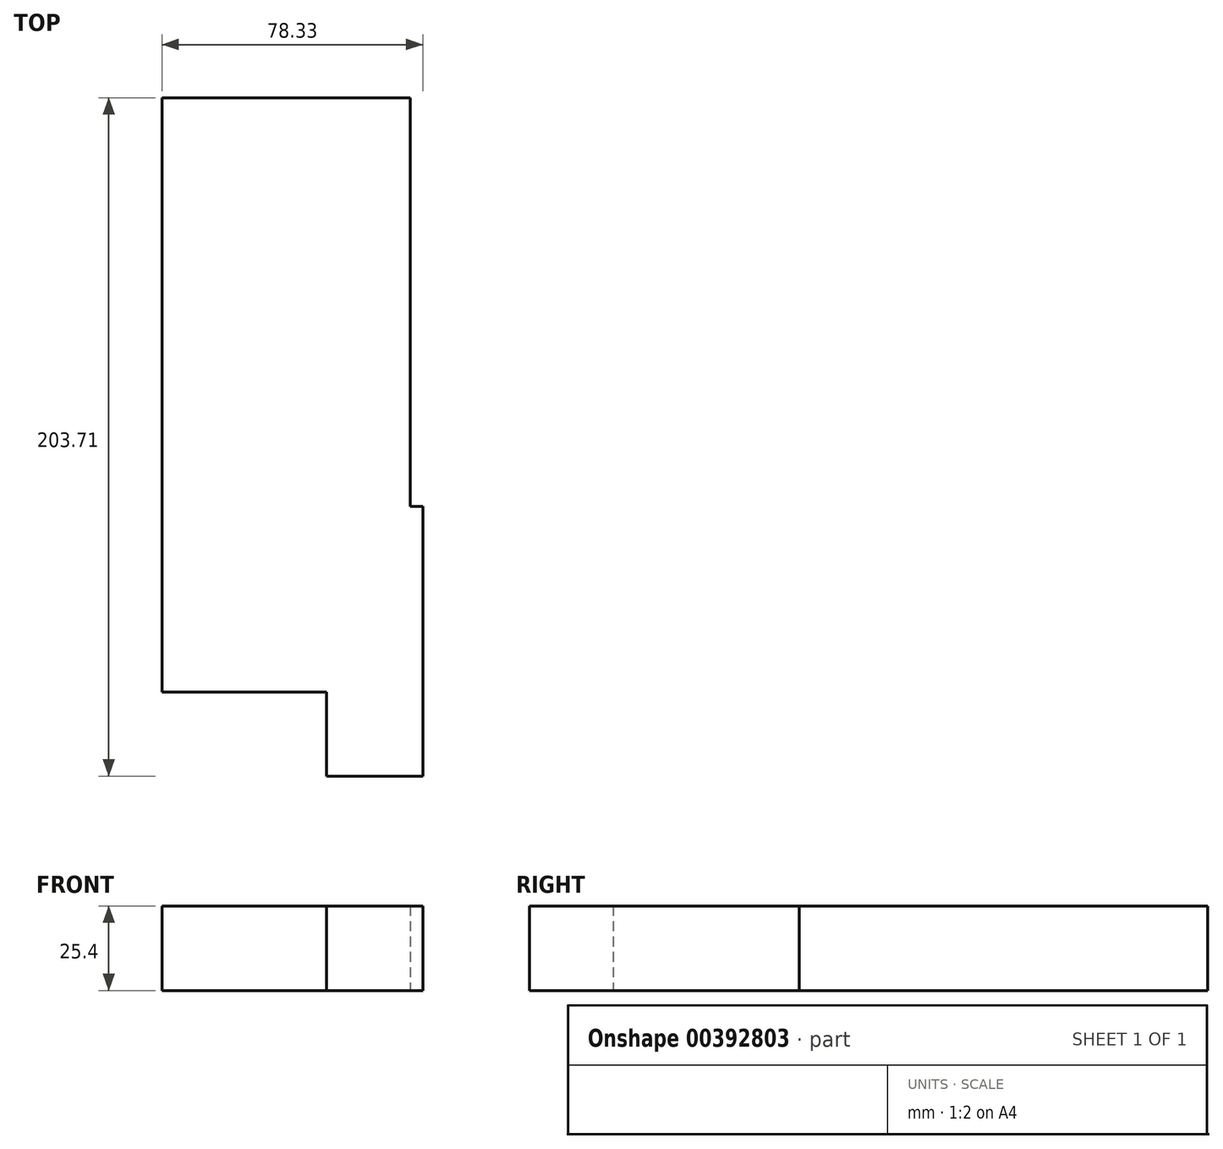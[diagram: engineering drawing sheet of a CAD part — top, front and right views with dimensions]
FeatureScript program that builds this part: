
annotation { "Feature Type Name" : "Feature", "Feature Type Description" : "" }
export const myFeature = defineFeature(function(context is Context, id is Id, definition is map)
    precondition{}
    {
        {
            var Q0;
            Q0=qCreatedBy(makeId("Top.planeOp"),FACE);
            var sketch = newSketch(context, id + "F0", { "sketchPlane" : qUnion([Q0])});
            skLineSegment(sketch, "E0.bottom", {"start": v(0, 82.52) * mm, "end": v(-74.5, 82.52) * mm});
            skLineSegment(sketch, "E0.top", {"start": v(0, 261.05) * mm, "end": v(-74.5, 261.05) * mm});
            skLineSegment(sketch, "E0.left", {"start": v(0, 82.52) * mm, "end": v(0, 261.05) * mm});
            skLineSegment(sketch, "E0.right", {"start": v(-74.5, 82.52) * mm, "end": v(-74.5, 261.05) * mm});
            skLineSegment(sketch, "E1.bottom", {"start": v(-25.05, 138.36) * mm, "end": v(3.84, 138.36) * mm});
            skLineSegment(sketch, "E1.top", {"start": v(-25.05, 57.34) * mm, "end": v(3.84, 57.34) * mm});
            skLineSegment(sketch, "E1.left", {"start": v(-25.05, 138.36) * mm, "end": v(-25.05, 57.34) * mm});
            skLineSegment(sketch, "E1.right", {"start": v(3.84, 138.36) * mm, "end": v(3.84, 57.34) * mm});
            skSolve(sketch);
        }
        {
            var Q0;
            Q0 = qSketchRegion(id + "F0", true);
            extrude(context, id + "F1", {"entities" : qUnion([Q0]), "depth" : 25.4 * mm});
        }
    });
